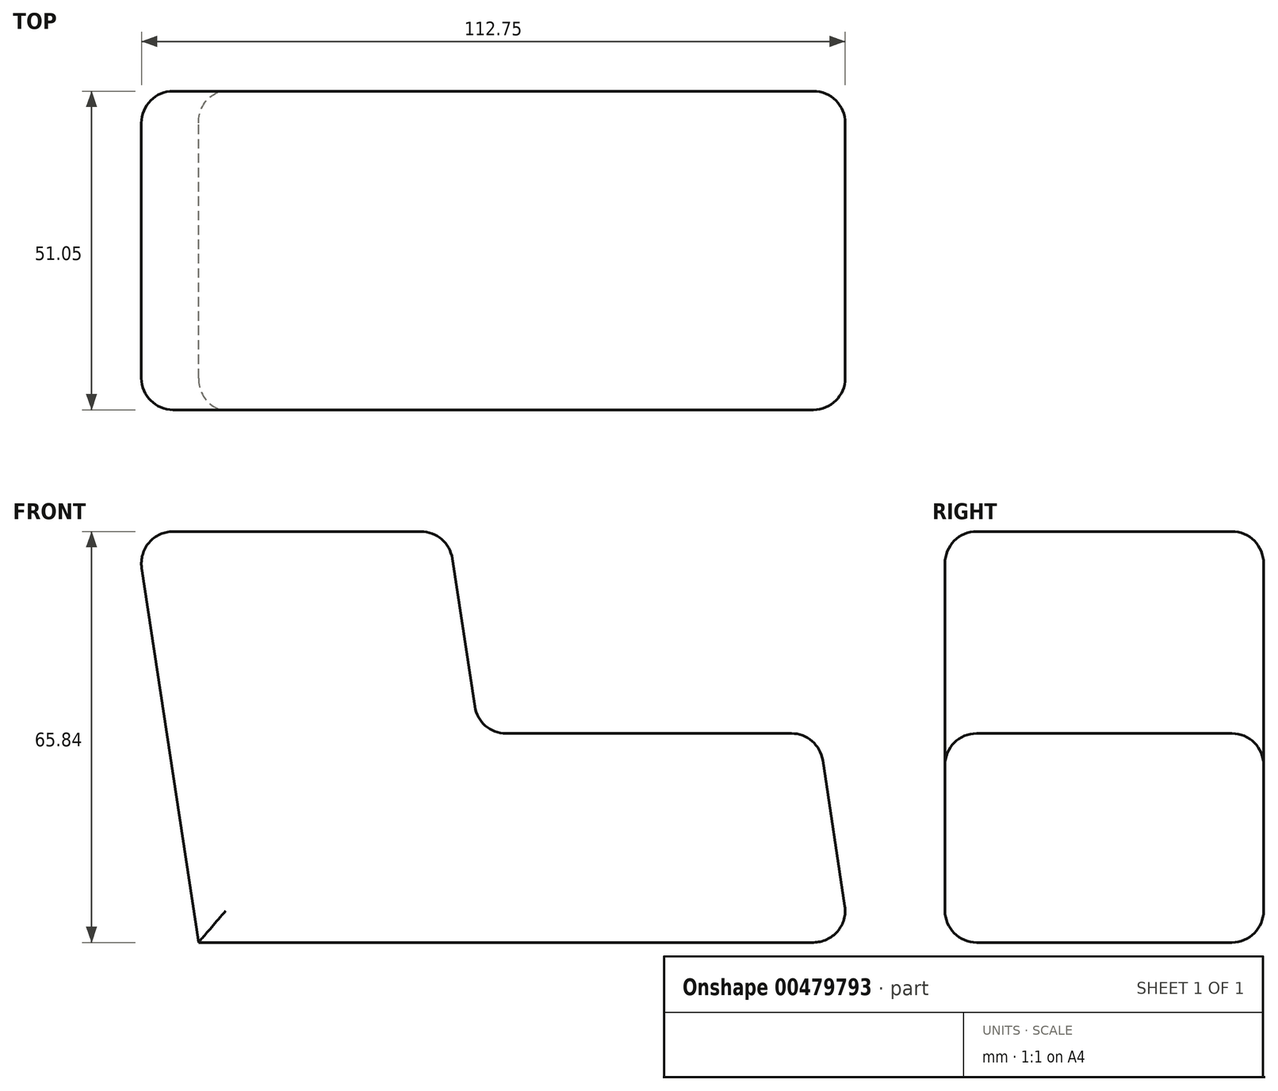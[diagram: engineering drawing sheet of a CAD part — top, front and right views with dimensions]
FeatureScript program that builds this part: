
annotation { "Feature Type Name" : "Feature", "Feature Type Description" : "" }
export const myFeature = defineFeature(function(context is Context, id is Id, definition is map)
    precondition{}
    {
        {
            var Q0;
            Q0=qCreatedBy(makeId("Front.planeOp"),FACE);
            var sketch = newSketch(context, id + "F0", { "sketchPlane" : qUnion([Q0])});
            skLineSegment(sketch, "E0", {"start": v(-64.3, 32.35) * mm, "end": v(-14.3, 32.35) * mm});
            skLineSegment(sketch, "E1", {"start": v(-14.3, 32.35) * mm, "end": v(-9.4, 0) * mm});
            skLineSegment(sketch, "E2", {"start": v(-9.4, 0) * mm, "end": v(45.04, 0) * mm});
            skLineSegment(sketch, "E3", {"start": v(45.04, 0) * mm, "end": v(50.11, -33.49) * mm});
            skLineSegment(sketch, "E4", {"start": v(50.11, -33.49) * mm, "end": v(-54.33, -33.49) * mm});
            skLineSegment(sketch, "E5", {"start": v(-54.33, -33.49) * mm, "end": v(-64.3, 32.35) * mm});
            skSolve(sketch);
        }
        {
            var Q0;
            Q0=makeQuery(id+"F0.imprint","IMPRINT",FACE,{"disambiguationData":[TD([[makeQuery(id+"F0.imprint","IMPRINT",EDGE,{"derivedFrom":sQuery(id+"F0.wireOp",EDGE,"E0")}),-1.0]])]});
            extrude(context, id + "F1", {"entities" : qUnion([Q0]), "depth" : 51.05 * mm});
        }
        {
            var Q0;
            Q0=makeQuery(id+"F1.opExtrude","CAP_FACE",FACE,{"disambiguationData":[OSD([sQuery(id+"F0.wireOp",EDGE,"E0"),sQuery(id+"F0.wireOp",EDGE,"E1"),sQuery(id+"F0.wireOp",EDGE,"E2"),sQuery(id+"F0.wireOp",EDGE,"E3"),sQuery(id+"F0.wireOp",EDGE,"E4"),sQuery(id+"F0.wireOp",EDGE,"E5")])],"isStart":false});
            var Q1;
            Q1=makeQuery(id+"F1.opExtrude","CAP_FACE",FACE,{"disambiguationData":[OSD([sQuery(id+"F0.wireOp",EDGE,"E0"),sQuery(id+"F0.wireOp",EDGE,"E1"),sQuery(id+"F0.wireOp",EDGE,"E2"),sQuery(id+"F0.wireOp",EDGE,"E3"),sQuery(id+"F0.wireOp",EDGE,"E4"),sQuery(id+"F0.wireOp",EDGE,"E5")])],"isStart":true});
            var Q2;
            Q2=makeQuery(id+"F1.opExtrude","SWEPT_FACE",FACE,{"disambiguationData":[OSD([sQuery(id+"F0.wireOp",EDGE,"E1")])]});
            var Q3;
            Q3=makeQuery(id+"F1.opExtrude","SWEPT_FACE",FACE,{"disambiguationData":[OSD([sQuery(id+"F0.wireOp",EDGE,"E2")])]});
            var Q4;
            Q4=makeQuery(id+"F1.opExtrude","SWEPT_FACE",FACE,{"disambiguationData":[OSD([sQuery(id+"F0.wireOp",EDGE,"E3")])]});
            var Q5;
            Q5=makeQuery(id+"F1.opExtrude","SWEPT_FACE",FACE,{"disambiguationData":[OSD([sQuery(id+"F0.wireOp",EDGE,"E0")])]});
            fillet(context, id + "F2", {"entities" : qUnion([Q0, Q1, Q2, Q3, Q4, Q5]), "radius" : 5.08 * mm, "tangentPropagation" : true, "allowEdgeOverflow" : false});
        }
    });
